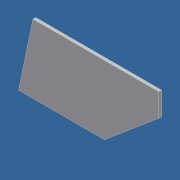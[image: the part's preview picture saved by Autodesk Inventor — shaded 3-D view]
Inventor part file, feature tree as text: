
AUTODESK INVENTOR PART (.ipt)
format: ipt  version: 2012 (Build 160160000, 160)  size: 68,096 bytes
history: native  units: in
note: dims shown in document units (in); Inventor stores cm internally (conversion verified against a paired STEP export)
features: extrude x1, sketch x1
ambient origin geometry x8: Origin, YZ Plane, XZ Plane, XY Plane, X Axis, Y Axis, Z Axis, Center Point
bodies: Solid1 (feature_tree)
feature tree (2):
  extrude  "Extrusion1"  Depth=11.0in
  sketch  "Sketch1"  dims[d0=6.0in d1=11.0in d2=2.0in d3=7.5in d4=1.25in d5=0.25in d6=0.0in]
